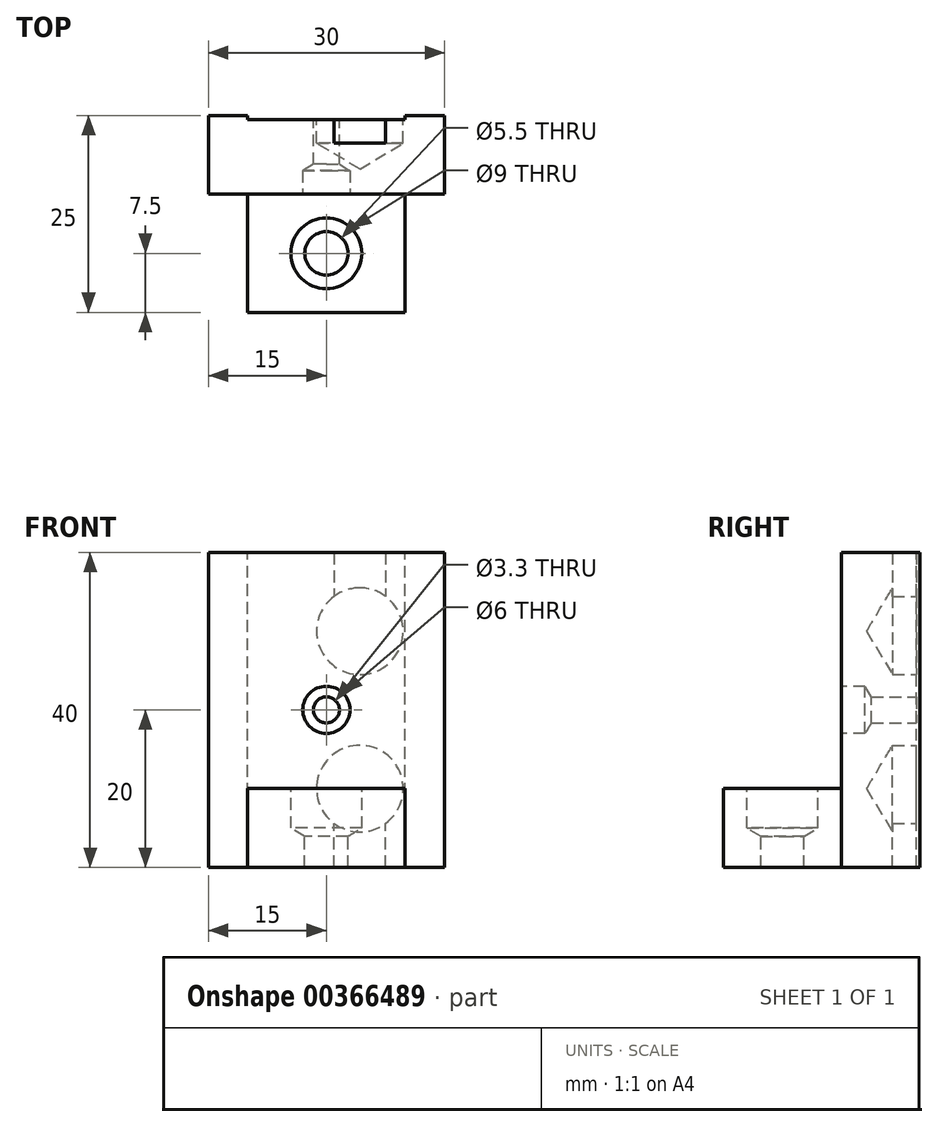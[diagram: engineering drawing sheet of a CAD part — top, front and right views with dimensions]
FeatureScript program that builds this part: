
annotation { "Feature Type Name" : "Feature", "Feature Type Description" : "" }
export const myFeature = defineFeature(function(context is Context, id is Id, definition is map)
    precondition{}
    {
        {
            var Q0;
            Q0=qCreatedBy(makeId("Front.planeOp"),FACE);
            var sketch = newSketch(context, id + "F0", { "sketchPlane" : qUnion([Q0])});
            skLineSegment(sketch, "E0.bottom", {"start": v(15, -20) * mm, "end": v(-15, -20) * mm});
            skLineSegment(sketch, "E0.top", {"start": v(15, 20) * mm, "end": v(-15, 20) * mm});
            skLineSegment(sketch, "E0.left", {"start": v(15, -20) * mm, "end": v(15, 20) * mm});
            skLineSegment(sketch, "E0.right", {"start": v(-15, -20) * mm, "end": v(-15, 20) * mm});
            skPoint(sketch, "E0.middle", {"position": v(0, 0) * mm});
            skSolve(sketch);
        }
        {
            var Q0;
            Q0=makeQuery(id+"F0.imprint","IMPRINT",FACE,{"disambiguationData":[TD([[makeQuery(id+"F0.imprint","IMPRINT",EDGE,{"derivedFrom":sQuery(id+"F0.wireOp",EDGE,"E0.bottom")}),-1.0]])]});
            extrude(context, id + "F1", {"entities" : qUnion([Q0]), "depth" : 10 * mm});
        }
        {
            var Q0;
            Q0=makeQuery(id+"F1.opExtrude","CAP_FACE",FACE,{"disambiguationData":[OSD([sQuery(id+"F0.wireOp",EDGE,"E0.bottom"),sQuery(id+"F0.wireOp",EDGE,"E0.top"),sQuery(id+"F0.wireOp",EDGE,"E0.left"),sQuery(id+"F0.wireOp",EDGE,"E0.right")])],"isStart":true});
            var sketch = newSketch(context, id + "F2", { "sketchPlane" : qUnion([Q0])});
            skLineSegment(sketch, "E1.bottom", {"start": v(10, -20) * mm, "end": v(-10, -20) * mm});
            skLineSegment(sketch, "E1.top", {"start": v(10, 20) * mm, "end": v(-10, 20) * mm});
            skLineSegment(sketch, "E1.left", {"start": v(10, -20) * mm, "end": v(10, 20) * mm});
            skLineSegment(sketch, "E1.right", {"start": v(-10, -20) * mm, "end": v(-10, 20) * mm});
            skPoint(sketch, "E1.middle", {"position": v(0, 0) * mm});
            skSolve(sketch);
        }
        {
            var Q0;
            Q0=makeQuery(id+"F2.imprint","IMPRINT",FACE,{"disambiguationData":[TD([[makeQuery(id+"F2.imprint","IMPRINT",EDGE,{"derivedFrom":sQuery(id+"F2.wireOp",EDGE,"E1.bottom")}),1.0]])]});
            extrude(context, id + "F3", {"entities" : qUnion([Q0]), "operationType" : NewBodyOperationType.REMOVE, "oppositeDirection" : true, "depth" : 0.5 * mm, "offsetDistance" : 25 * mm});
        }
        {
            var Q0;
            Q0=makeQuery(id+"F3.boolean.opBoolean","COPY",FACE,{"derivedFrom":makeQuery(id+"F3.opExtrude","CAP_FACE",FACE,{"disambiguationData":[OSD([sQuery(id+"F2.wireOp",EDGE,"E1.bottom"),sQuery(id+"F2.wireOp",EDGE,"E1.top"),sQuery(id+"F2.wireOp",EDGE,"E1.left"),sQuery(id+"F2.wireOp",EDGE,"E1.right")])],"isStart":false})});
            var sketch = newSketch(context, id + "F4", { "sketchPlane" : qUnion([Q0])});
            skLineSegment(sketch, "E2.bottom", {"start": v(-1, 20) * mm, "end": v(-7.5, 20) * mm});
            skLineSegment(sketch, "E2.top", {"start": v(-1, 10) * mm, "end": v(-7.5, 10) * mm});
            skLineSegment(sketch, "E2.left", {"start": v(-1, 20) * mm, "end": v(-1, 10) * mm});
            skLineSegment(sketch, "E2.right", {"start": v(-7.5, 20) * mm, "end": v(-7.5, 10) * mm});
            skSolve(sketch);
        }
        {
            var Q0;
            Q0=makeQuery(id+"F4.imprint","IMPRINT",FACE,{"disambiguationData":[TD([[makeQuery(id+"F4.imprint","IMPRINT",EDGE,{"derivedFrom":sQuery(id+"F4.wireOp",EDGE,"E2.bottom")}),-1.0]])]});
            extrude(context, id + "F5", {"entities" : qUnion([Q0]), "operationType" : NewBodyOperationType.REMOVE, "oppositeDirection" : true, "depth" : 3 * mm});
        }
        {
            var Q0;
            Q0=makeQuery(id+"F3.boolean.opBoolean","COPY",FACE,{"derivedFrom":makeQuery(id+"F3.opExtrude","CAP_FACE",FACE,{"disambiguationData":[OSD([sQuery(id+"F2.wireOp",EDGE,"E1.bottom"),sQuery(id+"F2.wireOp",EDGE,"E1.top"),sQuery(id+"F2.wireOp",EDGE,"E1.left"),sQuery(id+"F2.wireOp",EDGE,"E1.right")])],"isStart":false})});
            var sketch = newSketch(context, id + "F6", { "sketchPlane" : qUnion([Q0])});
            skLineSegment(sketch, "E3.bottom", {"start": v(-1, -20) * mm, "end": v(-7.5, -20) * mm});
            skLineSegment(sketch, "E3.top", {"start": v(-1, -10) * mm, "end": v(-7.5, -10) * mm});
            skLineSegment(sketch, "E3.left", {"start": v(-1, -20) * mm, "end": v(-1, -10) * mm});
            skLineSegment(sketch, "E3.right", {"start": v(-7.5, -20) * mm, "end": v(-7.5, -10) * mm});
            skSolve(sketch);
        }
        {
            var Q0;
            Q0=makeQuery(id+"F6.imprint","IMPRINT",FACE,{"disambiguationData":[TD([[makeQuery(id+"F6.imprint","IMPRINT",EDGE,{"derivedFrom":sQuery(id+"F6.wireOp",EDGE,"E3.bottom")}),1.0]])]});
            extrude(context, id + "F7", {"entities" : qUnion([Q0]), "operationType" : NewBodyOperationType.REMOVE, "oppositeDirection" : true, "depth" : 3 * mm});
        }
        {
            var Q0;
            Q0=makeQuery(id+"F1.opExtrude","CAP_FACE",FACE,{"disambiguationData":[OSD([sQuery(id+"F0.wireOp",EDGE,"E0.bottom"),sQuery(id+"F0.wireOp",EDGE,"E0.top"),sQuery(id+"F0.wireOp",EDGE,"E0.left"),sQuery(id+"F0.wireOp",EDGE,"E0.right")])],"isStart":false});
            var sketch = newSketch(context, id + "F8", { "sketchPlane" : qUnion([Q0])});
            skLineSegment(sketch, "E4.bottom", {"start": v(10, -20) * mm, "end": v(-10, -20) * mm});
            skLineSegment(sketch, "E4.top", {"start": v(10, -10) * mm, "end": v(-10, -10) * mm});
            skLineSegment(sketch, "E4.left", {"start": v(10, -20) * mm, "end": v(10, -10) * mm});
            skLineSegment(sketch, "E4.right", {"start": v(-10, -20) * mm, "end": v(-10, -10) * mm});
            skSolve(sketch);
        }
        {
            var Q0;
            Q0=makeQuery(id+"F8.imprint","IMPRINT",FACE,{"disambiguationData":[TD([[makeQuery(id+"F8.imprint","IMPRINT",EDGE,{"derivedFrom":sQuery(id+"F8.wireOp",EDGE,"E4.bottom")}),-1.0]])]});
            extrude(context, id + "F9", {"entities" : qUnion([Q0]), "operationType" : NewBodyOperationType.ADD, "depth" : 15 * mm});
        }
        {
            var Q0;
            Q0=makeQuery(id+"F9.opExtrude","SWEPT_FACE",FACE,{"disambiguationData":[OSD([sQuery(id+"F8.wireOp",EDGE,"E4.top")])]});
            var sketch = newSketch(context, id + "F10", { "sketchPlane" : qUnion([Q0])});
            skPoint(sketch, "E5", {"position": v(0, -17.5) * mm});
            skPoint(sketch, "E5.positionSnap0", {"position": v(10, -17.5) * mm});
            skSolve(sketch);
        }
        {
            var Q0;
            Q0=sQuery(id+"F10.wireOp",VERTEX,"E5");
            var Q1;
            Q1=makeQuery(id+"F1.opExtrude","SWEPT_BODY",BODY,{"disambiguationData":[OSD([sQuery(id+"F0.wireOp",EDGE,"E0.bottom"),sQuery(id+"F0.wireOp",EDGE,"E0.top"),sQuery(id+"F0.wireOp",EDGE,"E0.left"),sQuery(id+"F0.wireOp",EDGE,"E0.right")])]});
            hole(context, id + "F11", {"style" : HoleStyle.SIMPLE, "endStyle" : HoleEndStyle.THROUGH, "standardTappedOrClearance" : lookupTablePath({ "standard" : "ISO", "fit" : "Normal", "size" : "M5", "type" : "Clearance" }), "standardBlindInLast" : lookupTablePath({ "fit" : "Standard", "standard" : "ISO", "size" : "M5", "type" : "Clearance" }), "holeDiameter" : 5.5 * mm, "isTappedThrough" : true, "tappedDepth" : 12 * mm, "tapClearance" : 3, "startFromSketch" : true, "locations" : qUnion([Q0]), "scope" : qUnion([Q1])});
        }
        {
            var Q0;
            Q0=makeQuery(id+"F9.opExtrude","SWEPT_FACE",FACE,{"disambiguationData":[OSD([sQuery(id+"F8.wireOp",EDGE,"E4.top")])]});
            var sketch = newSketch(context, id + "F12", { "sketchPlane" : qUnion([Q0])});
            skPoint(sketch, "E6", {"position": v(0, -17.5) * mm});
            skSolve(sketch);
        }
        {
            var Q0;
            Q0=sQuery(id+"F12.wireOp",VERTEX,"E6");
            var Q1;
            Q1=makeQuery(id+"F1.opExtrude","SWEPT_BODY",BODY,{"disambiguationData":[OSD([sQuery(id+"F0.wireOp",EDGE,"E0.bottom"),sQuery(id+"F0.wireOp",EDGE,"E0.top"),sQuery(id+"F0.wireOp",EDGE,"E0.left"),sQuery(id+"F0.wireOp",EDGE,"E0.right")])]});
            hole(context, id + "F13", {"style" : HoleStyle.SIMPLE, "endStyle" : HoleEndStyle.BLIND, "holeDiameter" : 9 * mm, "holeDepth" : 5 * mm, "isTappedThrough" : true, "tappedDepth" : 12 * mm, "tapClearance" : 3, "startFromSketch" : true, "locations" : qUnion([Q0]), "scope" : qUnion([Q1])});
        }
        {
            var Q0;
            Q0=makeQuery(id+"F3.boolean.opBoolean","COPY",FACE,{"derivedFrom":makeQuery(id+"F3.opExtrude","CAP_FACE",FACE,{"disambiguationData":[OSD([sQuery(id+"F2.wireOp",EDGE,"E1.bottom"),sQuery(id+"F2.wireOp",EDGE,"E1.top"),sQuery(id+"F2.wireOp",EDGE,"E1.left"),sQuery(id+"F2.wireOp",EDGE,"E1.right")])],"isStart":false})});
            var sketch = newSketch(context, id + "F14", { "sketchPlane" : qUnion([Q0])});
            skPoint(sketch, "E7", {"position": v(-4.25, 10) * mm});
            skSolve(sketch);
        }
        {
            var Q0;
            Q0=sQuery(id+"F14.wireOp",VERTEX,"E7");
            var Q1;
            Q1=makeQuery(id+"F1.opExtrude","SWEPT_BODY",BODY,{"disambiguationData":[OSD([sQuery(id+"F0.wireOp",EDGE,"E0.bottom"),sQuery(id+"F0.wireOp",EDGE,"E0.top"),sQuery(id+"F0.wireOp",EDGE,"E0.left"),sQuery(id+"F0.wireOp",EDGE,"E0.right")])]});
            hole(context, id + "F15", {"style" : HoleStyle.SIMPLE, "endStyle" : HoleEndStyle.BLIND, "holeDiameter" : 11 * mm, "holeDepth" : 3 * mm, "isTappedThrough" : true, "tappedDepth" : 12 * mm, "tapClearance" : 3, "startFromSketch" : true, "locations" : qUnion([Q0]), "scope" : qUnion([Q1])});
        }
        {
            var Q0;
            Q0=makeQuery(id+"F3.boolean.opBoolean","COPY",FACE,{"derivedFrom":makeQuery(id+"F3.opExtrude","CAP_FACE",FACE,{"disambiguationData":[OSD([sQuery(id+"F2.wireOp",EDGE,"E1.bottom"),sQuery(id+"F2.wireOp",EDGE,"E1.top"),sQuery(id+"F2.wireOp",EDGE,"E1.left"),sQuery(id+"F2.wireOp",EDGE,"E1.right")])],"isStart":false})});
            var sketch = newSketch(context, id + "F16", { "sketchPlane" : qUnion([Q0])});
            skPoint(sketch, "E8", {"position": v(-4.25, -10) * mm});
            skSolve(sketch);
        }
        {
            var Q0;
            Q0=sQuery(id+"F16.wireOp",VERTEX,"E8");
            var Q1;
            Q1=makeQuery(id+"F1.opExtrude","SWEPT_BODY",BODY,{"disambiguationData":[OSD([sQuery(id+"F0.wireOp",EDGE,"E0.bottom"),sQuery(id+"F0.wireOp",EDGE,"E0.top"),sQuery(id+"F0.wireOp",EDGE,"E0.left"),sQuery(id+"F0.wireOp",EDGE,"E0.right")])]});
            hole(context, id + "F17", {"style" : HoleStyle.SIMPLE, "endStyle" : HoleEndStyle.BLIND, "holeDiameter" : 11 * mm, "holeDepth" : 3 * mm, "isTappedThrough" : true, "tappedDepth" : 12 * mm, "tapClearance" : 3, "startFromSketch" : true, "locations" : qUnion([Q0]), "scope" : qUnion([Q1])});
        }
        {
            var Q0;
            Q0=makeQuery(id+"F3.boolean.opBoolean","COPY",FACE,{"derivedFrom":makeQuery(id+"F3.opExtrude","CAP_FACE",FACE,{"disambiguationData":[OSD([sQuery(id+"F2.wireOp",EDGE,"E1.bottom"),sQuery(id+"F2.wireOp",EDGE,"E1.top"),sQuery(id+"F2.wireOp",EDGE,"E1.left"),sQuery(id+"F2.wireOp",EDGE,"E1.right")])],"isStart":false})});
            var sketch = newSketch(context, id + "F18", { "sketchPlane" : qUnion([Q0])});
            skPoint(sketch, "E9", {"position": v(0, 0) * mm});
            skSolve(sketch);
        }
        {
            var Q0;
            Q0=sQuery(id+"F18.wireOp",VERTEX,"E9");
            var Q1;
            Q1=makeQuery(id+"F1.opExtrude","SWEPT_BODY",BODY,{"disambiguationData":[OSD([sQuery(id+"F0.wireOp",EDGE,"E0.bottom"),sQuery(id+"F0.wireOp",EDGE,"E0.top"),sQuery(id+"F0.wireOp",EDGE,"E0.left"),sQuery(id+"F0.wireOp",EDGE,"E0.right")])]});
            hole(context, id + "F19", {"style" : HoleStyle.SIMPLE, "endStyle" : HoleEndStyle.BLIND, "standardTappedOrClearance" : lookupTablePath({ "standard" : "ISO", "fit" : "Normal", "size" : "M3", "type" : "Clearance" }), "standardBlindInLast" : lookupTablePath({ "fit" : "Standard", "standard" : "ISO", "size" : "M3", "type" : "Clearance" }), "holeDiameter" : 3.3 * mm, "holeDepth" : 30 * mm, "isTappedThrough" : true, "tappedDepth" : 12 * mm, "tapClearance" : 3, "startFromSketch" : true, "locations" : qUnion([Q0]), "scope" : qUnion([Q1])});
        }
        {
            var Q0;
            Q0=makeQuery(id+"F1.opExtrude","CAP_FACE",FACE,{"disambiguationData":[OSD([sQuery(id+"F0.wireOp",EDGE,"E0.bottom"),sQuery(id+"F0.wireOp",EDGE,"E0.top"),sQuery(id+"F0.wireOp",EDGE,"E0.left"),sQuery(id+"F0.wireOp",EDGE,"E0.right")])],"isStart":false});
            var sketch = newSketch(context, id + "F20", { "sketchPlane" : qUnion([Q0])});
            skPoint(sketch, "E10", {"position": v(0, 0) * mm});
            skSolve(sketch);
        }
        {
            var Q0;
            Q0=sQuery(id+"F20.wireOp",VERTEX,"E10");
            var Q1;
            Q1=makeQuery(id+"F1.opExtrude","SWEPT_BODY",BODY,{"disambiguationData":[OSD([sQuery(id+"F0.wireOp",EDGE,"E0.bottom"),sQuery(id+"F0.wireOp",EDGE,"E0.top"),sQuery(id+"F0.wireOp",EDGE,"E0.left"),sQuery(id+"F0.wireOp",EDGE,"E0.right")])]});
            hole(context, id + "F21", {"style" : HoleStyle.SIMPLE, "endStyle" : HoleEndStyle.BLIND, "holeDiameter" : 6 * mm, "holeDepth" : 3 * mm, "isTappedThrough" : true, "tappedDepth" : 12 * mm, "tapClearance" : 3, "startFromSketch" : true, "locations" : qUnion([Q0]), "scope" : qUnion([Q1])});
        }
    });
